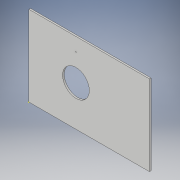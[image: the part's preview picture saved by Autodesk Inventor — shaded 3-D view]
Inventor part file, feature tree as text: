
AUTODESK INVENTOR PART (.ipt)
format: ipt  version: 2017 (Build 210142000, 142)  size: 101,376 bytes
history: native  units: in
note: dims shown in document units (in); Inventor stores cm internally (conversion verified against a paired STEP export)
features: sketch x3, extrude x1
ambient origin geometry x8: Origin, YZ Plane, XZ Plane, XY Plane, X Axis, Y Axis, Z Axis, Center Point
bodies: Body1 (feature_tree)
feature tree (4):
  sketch  "Sketch1"  dims[d0=18.0in d1=12.0in]
  sketch  "Sketch2"  dims[d4=4.0in]
  extrude  "Extrusion2"  Depth=12.0in
  sketch  "Sketch3"  dims[d8=0.25in d9=0.0in]
